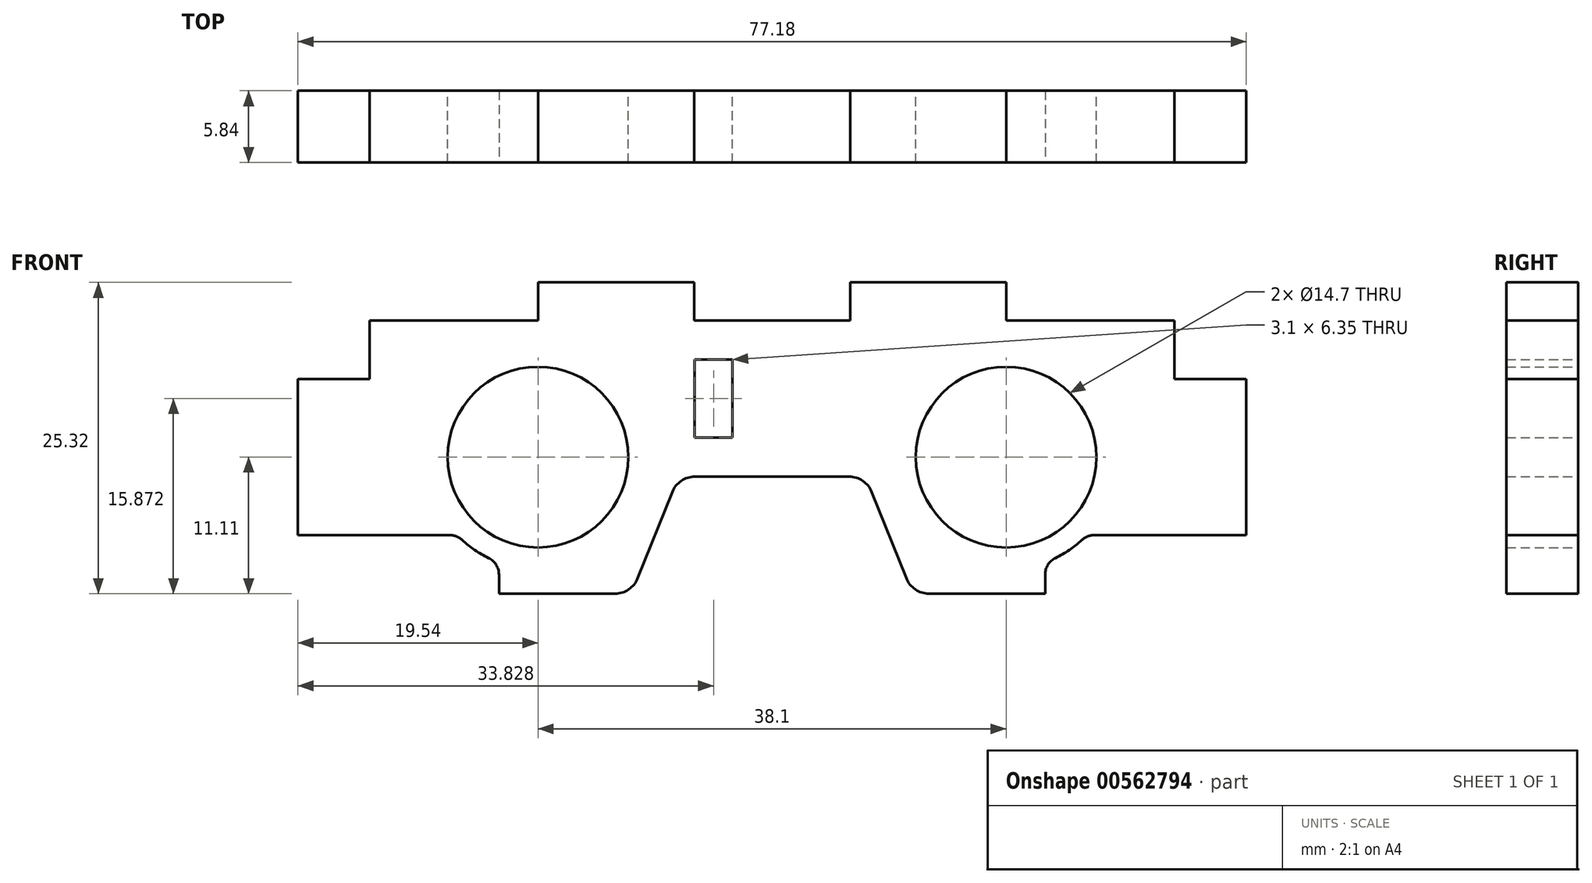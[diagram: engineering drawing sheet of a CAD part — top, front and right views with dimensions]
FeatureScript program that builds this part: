
annotation { "Feature Type Name" : "Feature", "Feature Type Description" : "" }
export const myFeature = defineFeature(function(context is Context, id is Id, definition is map)
    precondition{}
    {
        {
            var Q0;
            Q0=qCreatedBy(makeId("Front.planeOp"),FACE);
            var sketch = newSketch(context, id + "F0", { "sketchPlane" : qUnion([Q0])});
            skCircle(sketch, "E0", {"center": v(-19.05, 0) * mm, "radius": 7.35 * mm});
            skCircle(sketch, "E1.MirrorC", {"center": v(19.05, 0) * mm, "radius": 7.35 * mm});
            skLineSegment(sketch, "E2.bottom", {"start": v(-31.75, 11.11) * mm, "end": v(31.75, 11.11) * mm});
            skLineSegment(sketch, "E2.top", {"start": v(-31.75, -11.11) * mm, "end": v(-11.43, -11.11) * mm});
            skLineSegment(sketch, "E2.left", {"start": v(-31.75, 11.11) * mm, "end": v(-31.75, -11.11) * mm});
            skLineSegment(sketch, "E2.right", {"start": v(31.75, 11.11) * mm, "end": v(31.75, -11.11) * mm});
            skPoint(sketch, "E2.middle", {"position": v(0, 0) * mm});
            skLineSegment(sketch, "E3", {"start": v(-11.43, -11.11) * mm, "end": v(-7.62, -1.59) * mm});
            skLineSegment(sketch, "E4", {"start": v(-7.62, -1.59) * mm, "end": v(0, -1.59) * mm});
            skLineSegment(sketch, "E5.MirrorCS", {"start": v(7.62, -1.59) * mm, "end": v(0, -1.59) * mm});
            skLineSegment(sketch, "E6.MirrorCS", {"start": v(11.43, -11.11) * mm, "end": v(7.62, -1.59) * mm});
            skLineSegment(sketch, "E7.trimOffspring", {"start": v(11.43, -11.11) * mm, "end": v(31.75, -11.11) * mm});
            skSolve(sketch);
        }
        {
            var Q0;
            Q0=makeQuery(id+"F0.imprint","IMPRINT",FACE,{"disambiguationData":[TD([[makeQuery(id+"F0.imprint","IMPRINT",EDGE,{"derivedFrom":sQuery(id+"F0.wireOp",EDGE,"E0")}),-1.0]])]});
            extrude(context, id + "F1", {"entities" : qUnion([Q0]), "depth" : 5.84 * mm, "offsetDistance" : 25.4 * mm});
        }
        {
            var Q0;
            Q0=makeQuery(id+"F1.opExtrude","SWEPT_EDGE",EDGE,{"disambiguationData":[OSD([sQuery(id+"F0.wireOp",EDGE,"E2.top"),sQuery(id+"F0.wireOp",EDGE,"E3")])]});
            var Q1;
            Q1=makeQuery(id+"F1.opExtrude","SWEPT_EDGE",EDGE,{"disambiguationData":[OSD([sQuery(id+"F0.wireOp",EDGE,"E3"),sQuery(id+"F0.wireOp",EDGE,"E4")])]});
            var Q2;
            Q2=makeQuery(id+"F1.opExtrude","SWEPT_EDGE",EDGE,{"disambiguationData":[OSD([sQuery(id+"F0.wireOp",EDGE,"E5.MirrorCS"),sQuery(id+"F0.wireOp",EDGE,"E6.MirrorCS")])]});
            var Q3;
            Q3=makeQuery(id+"F1.opExtrude","SWEPT_EDGE",EDGE,{"disambiguationData":[OSD([sQuery(id+"F0.wireOp",EDGE,"E6.MirrorCS"),sQuery(id+"F0.wireOp",EDGE,"E7.trimOffspring")])]});
            fillet(context, id + "F2", {"entities" : qUnion([Q0, Q1, Q2, Q3]), "radius" : 2 * mm, "tangentPropagation" : true, "allowEdgeOverflow" : false});
        }
        {
            var Q0;
            Q0=makeQuery(id+"F1.opExtrude","CAP_FACE",FACE,{"disambiguationData":[OSD([sQuery(id+"F0.wireOp",EDGE,"E0"),sQuery(id+"F0.wireOp",EDGE,"E1.MirrorC"),sQuery(id+"F0.wireOp",EDGE,"E2.bottom"),sQuery(id+"F0.wireOp",EDGE,"E2.top"),sQuery(id+"F0.wireOp",EDGE,"E2.left"),sQuery(id+"F0.wireOp",EDGE,"E2.right"),sQuery(id+"F0.wireOp",EDGE,"E3"),sQuery(id+"F0.wireOp",EDGE,"E4"),sQuery(id+"F0.wireOp",EDGE,"E5.MirrorCS"),sQuery(id+"F0.wireOp",EDGE,"E6.MirrorCS"),sQuery(id+"F0.wireOp",EDGE,"E7.trimOffspring")])],"isStart":true});
            var sketch = newSketch(context, id + "F3", { "sketchPlane" : qUnion([Q0])});
            skLineSegment(sketch, "E8.bottom", {"start": v(6.31, 1.59) * mm, "end": v(3.21, 1.59) * mm});
            skLineSegment(sketch, "E8.top", {"start": v(6.31, 7.94) * mm, "end": v(3.21, 7.94) * mm});
            skLineSegment(sketch, "E8.left", {"start": v(6.31, 1.59) * mm, "end": v(6.31, 7.94) * mm});
            skLineSegment(sketch, "E8.right", {"start": v(3.21, 1.59) * mm, "end": v(3.21, 7.94) * mm});
            skPoint(sketch, "E8.middle", {"position": v(4.76, 4.76) * mm});
            skSolve(sketch);
        }
        {
            var Q0;
            Q0=qSketchRegion(id+"F3",true);
            extrude(context, id + "F4", {"entities" : qUnion([Q0]), "operationType" : NewBodyOperationType.REMOVE, "oppositeDirection" : true, "depth" : 25.4 * mm, "offsetDistance" : 25.4 * mm});
        }
        {
            var Q0;
            Q0=makeQuery(id+"F1.opExtrude","CAP_FACE",FACE,{"disambiguationData":[OSD([sQuery(id+"F0.wireOp",EDGE,"E0"),sQuery(id+"F0.wireOp",EDGE,"E1.MirrorC"),sQuery(id+"F0.wireOp",EDGE,"E2.bottom"),sQuery(id+"F0.wireOp",EDGE,"E2.top"),sQuery(id+"F0.wireOp",EDGE,"E2.left"),sQuery(id+"F0.wireOp",EDGE,"E2.right"),sQuery(id+"F0.wireOp",EDGE,"E3"),sQuery(id+"F0.wireOp",EDGE,"E4"),sQuery(id+"F0.wireOp",EDGE,"E5.MirrorCS"),sQuery(id+"F0.wireOp",EDGE,"E6.MirrorCS"),sQuery(id+"F0.wireOp",EDGE,"E7.trimOffspring")])],"isStart":false});
            var sketch = newSketch(context, id + "F5", { "sketchPlane" : qUnion([Q0])});
            skLineSegment(sketch, "E9.bottom", {"start": v(-19.05, 11.11) * mm, "end": v(-6.35, 11.11) * mm});
            skLineSegment(sketch, "E9.top", {"start": v(-19.05, 14.21) * mm, "end": v(-6.35, 14.21) * mm});
            skLineSegment(sketch, "E9.left", {"start": v(-19.05, 11.11) * mm, "end": v(-19.05, 14.21) * mm});
            skLineSegment(sketch, "E9.right", {"start": v(-6.35, 11.11) * mm, "end": v(-6.35, 14.21) * mm});
            skPoint(sketch, "E9.middle", {"position": v(-12.7, 12.66) * mm});
            skLineSegment(sketch, "E10.MirrorCS", {"start": v(19.05, 11.11) * mm, "end": v(19.05, 14.21) * mm});
            skLineSegment(sketch, "E11.MirrorCS", {"start": v(19.05, 14.21) * mm, "end": v(6.35, 14.21) * mm});
            skLineSegment(sketch, "E12.MirrorCS", {"start": v(19.05, 11.11) * mm, "end": v(6.35, 11.11) * mm});
            skPoint(sketch, "E13.MirrorP", {"position": v(12.7, 12.66) * mm});
            skLineSegment(sketch, "E14.MirrorCS", {"start": v(6.35, 11.11) * mm, "end": v(6.35, 14.21) * mm});
            skSolve(sketch);
        }
        {
            var Q0;
            Q0=qSketchRegion(id+"F5",true);
            var Q1;
            Q1=makeQuery(id+"F1.opExtrude","CAP_FACE",FACE,{"disambiguationData":[OSD([sQuery(id+"F0.wireOp",EDGE,"E0"),sQuery(id+"F0.wireOp",EDGE,"E1.MirrorC"),sQuery(id+"F0.wireOp",EDGE,"E2.bottom"),sQuery(id+"F0.wireOp",EDGE,"E2.top"),sQuery(id+"F0.wireOp",EDGE,"E2.left"),sQuery(id+"F0.wireOp",EDGE,"E2.right"),sQuery(id+"F0.wireOp",EDGE,"E3"),sQuery(id+"F0.wireOp",EDGE,"E4"),sQuery(id+"F0.wireOp",EDGE,"E5.MirrorCS"),sQuery(id+"F0.wireOp",EDGE,"E6.MirrorCS"),sQuery(id+"F0.wireOp",EDGE,"E7.trimOffspring")])],"isStart":true});
            extrude(context, id + "F6", {"entities" : qUnion([Q0]), "operationType" : NewBodyOperationType.ADD, "endBound" : BoundingType.UP_TO_SURFACE, "oppositeDirection" : true, "depth" : 25.4 * mm, "endBoundEntityFace" : qUnion([Q1]), "offsetDistance" : 25.4 * mm});
        }
        {
            var Q0;
            Q0=makeQuery(id+"F6.boolean.opBoolean","MERGE",FACE,{"derivedFrom":[makeQuery(id+"F1.opExtrude","CAP_FACE",FACE,{"disambiguationData":[OSD([sQuery(id+"F0.wireOp",EDGE,"E0"),sQuery(id+"F0.wireOp",EDGE,"E1.MirrorC"),sQuery(id+"F0.wireOp",EDGE,"E2.bottom"),sQuery(id+"F0.wireOp",EDGE,"E2.top"),sQuery(id+"F0.wireOp",EDGE,"E2.left"),sQuery(id+"F0.wireOp",EDGE,"E2.right"),sQuery(id+"F0.wireOp",EDGE,"E3"),sQuery(id+"F0.wireOp",EDGE,"E4"),sQuery(id+"F0.wireOp",EDGE,"E5.MirrorCS"),sQuery(id+"F0.wireOp",EDGE,"E6.MirrorCS"),sQuery(id+"F0.wireOp",EDGE,"E7.trimOffspring")])],"isStart":false}),makeQuery(id+"F6.opExtrude","CAP_FACE",FACE,{"disambiguationData":[OSD([sQuery(id+"F5.wireOp",EDGE,"E9.bottom"),sQuery(id+"F5.wireOp",EDGE,"E9.top"),sQuery(id+"F5.wireOp",EDGE,"E9.left"),sQuery(id+"F5.wireOp",EDGE,"E9.right")])],"isStart":true}),makeQuery(id+"F6.opExtrude","CAP_FACE",FACE,{"disambiguationData":[OSD([sQuery(id+"F5.wireOp",EDGE,"E10.MirrorCS"),sQuery(id+"F5.wireOp",EDGE,"E11.MirrorCS"),sQuery(id+"F5.wireOp",EDGE,"E12.MirrorCS"),sQuery(id+"F5.wireOp",EDGE,"E14.MirrorCS")])],"isStart":true})]});
            var sketch = newSketch(context, id + "F7", { "sketchPlane" : qUnion([Q0])});
            skLineSegment(sketch, "E15.bottom", {"start": v(32.75, 6.35) * mm, "end": v(38.6, 6.35) * mm});
            skLineSegment(sketch, "E15.top", {"start": v(32.75, -6.35) * mm, "end": v(38.6, -6.35) * mm});
            skLineSegment(sketch, "E15.left", {"start": v(31.75, 6.35) * mm, "end": v(31.75, -6.35) * mm});
            skLineSegment(sketch, "E15.right", {"start": v(38.6, 6.35) * mm, "end": v(38.6, -6.35) * mm});
            skPoint(sketch, "E15.middle", {"position": v(35.17, 0) * mm});
            skPoint(sketch, "E16.MirrorP", {"position": v(-35.17, 0) * mm});
            skLineSegment(sketch, "E17.bottom", {"start": v(31.75, 11.11) * mm, "end": v(32.75, 11.11) * mm});
            skLineSegment(sketch, "E17.top", {"start": v(31.75, -11.11) * mm, "end": v(32.75, -11.11) * mm});
            skLineSegment(sketch, "E17.left", {"start": v(31.75, 11.11) * mm, "end": v(31.75, -11.11) * mm});
            skLineSegment(sketch, "E17.right", {"start": v(32.75, 11.11) * mm, "end": v(32.75, 6.35) * mm});
            skLineSegment(sketch, "E18.trimOffspring", {"start": v(32.75, -6.35) * mm, "end": v(32.75, -11.11) * mm});
            skPoint(sketch, "E19.MirrorCS.start.orphan", {"position": v(-38.6, 6.35) * mm});
            skPoint(sketch, "E20.MirrorCS.start.orphan", {"position": v(-31.75, 6.35) * mm});
            skPoint(sketch, "E21.MirrorCS.end.orphan", {"position": v(-38.6, -6.35) * mm});
            skPoint(sketch, "E21.MirrorCS.start.orphan", {"position": v(-31.75, -6.35) * mm});
            skLineSegment(sketch, "E22.MirrorCS", {"start": v(-31.75, 11.11) * mm, "end": v(-32.75, 11.11) * mm});
            skLineSegment(sketch, "E23.MirrorCS", {"start": v(-31.75, -11.11) * mm, "end": v(-32.75, -11.11) * mm});
            skLineSegment(sketch, "E24.MirrorCS", {"start": v(-31.75, 6.35) * mm, "end": v(-31.75, -6.35) * mm});
            skLineSegment(sketch, "E25.MirrorCS", {"start": v(-32.75, -6.35) * mm, "end": v(-32.75, -11.11) * mm});
            skLineSegment(sketch, "E26.MirrorCS", {"start": v(-32.75, 11.11) * mm, "end": v(-32.75, 6.35) * mm});
            skLineSegment(sketch, "E27.MirrorCS", {"start": v(-32.75, -6.35) * mm, "end": v(-38.6, -6.35) * mm});
            skLineSegment(sketch, "E28.MirrorCS", {"start": v(-32.75, 6.35) * mm, "end": v(-38.6, 6.35) * mm});
            skLineSegment(sketch, "E29.MirrorCS", {"start": v(-38.6, 6.35) * mm, "end": v(-38.6, -6.35) * mm});
            skLineSegment(sketch, "E30.MirrorCS", {"start": v(-31.75, 11.11) * mm, "end": v(-31.75, -11.11) * mm});
            skSolve(sketch);
        }
        {
            var Q0;
            Q0=qSketchRegion(id+"F7",true);
            var Q1;
            {var subQ0=sQuery(id+"F0.wireOp",EDGE,"E7.trimOffspring");var subQ1=sQuery(id+"F0.wireOp",EDGE,"E6.MirrorCS");var subQ2=sQuery(id+"F0.wireOp",EDGE,"E5.MirrorCS");var subQ3=sQuery(id+"F0.wireOp",EDGE,"E4");var subQ4=sQuery(id+"F0.wireOp",EDGE,"E3");var subQ5=sQuery(id+"F0.wireOp",EDGE,"E2.right");var subQ6=sQuery(id+"F0.wireOp",EDGE,"E2.left");var subQ7=sQuery(id+"F0.wireOp",EDGE,"E2.top");var subQ8=sQuery(id+"F0.wireOp",EDGE,"E2.bottom");var subQ9=sQuery(id+"F0.wireOp",EDGE,"E1.MirrorC");var subQ10=sQuery(id+"F0.wireOp",EDGE,"E0");Q1=makeQuery(id+"F6.boolean.opBoolean","MERGE",FACE,{"derivedFrom":[makeQuery(id+"F1.opExtrude","CAP_FACE",FACE,{"disambiguationData":[OSD([subQ10,subQ9,subQ8,subQ7,subQ6,subQ5,subQ4,subQ3,subQ2,subQ1,subQ0])],"isStart":true}),makeQuery(id+"F6.opExtrude","CAP_FACE",FACE,{"disambiguationData":[OSD([subQ10,subQ9,subQ8,subQ7,subQ6,subQ5,subQ4,subQ3,subQ2,subQ1,subQ0]),OD(0.0)],"isStart":false}),makeQuery(id+"F6.opExtrude","CAP_FACE",FACE,{"disambiguationData":[OSD([subQ10,subQ9,subQ8,subQ7,subQ6,subQ5,subQ4,subQ3,subQ2,subQ1,subQ0]),OD(1.0)],"isStart":false})]});}
            extrude(context, id + "F8", {"entities" : qUnion([Q0]), "operationType" : NewBodyOperationType.ADD, "endBound" : BoundingType.UP_TO_SURFACE, "oppositeDirection" : true, "depth" : 25.4 * mm, "endBoundEntityFace" : qUnion([Q1]), "offsetDistance" : 25.4 * mm});
        }
        {
            var Q0;
            Q0=makeQuery(id+"F8.boolean.opBoolean","MERGE",FACE,{"derivedFrom":[makeQuery(id+"F6.boolean.opBoolean","MERGE",FACE,{"derivedFrom":[makeQuery(id+"F1.opExtrude","CAP_FACE",FACE,{"disambiguationData":[OSD([sQuery(id+"F0.wireOp",EDGE,"E0"),sQuery(id+"F0.wireOp",EDGE,"E1.MirrorC"),sQuery(id+"F0.wireOp",EDGE,"E2.bottom"),sQuery(id+"F0.wireOp",EDGE,"E2.top"),sQuery(id+"F0.wireOp",EDGE,"E2.left"),sQuery(id+"F0.wireOp",EDGE,"E2.right"),sQuery(id+"F0.wireOp",EDGE,"E3"),sQuery(id+"F0.wireOp",EDGE,"E4"),sQuery(id+"F0.wireOp",EDGE,"E5.MirrorCS"),sQuery(id+"F0.wireOp",EDGE,"E6.MirrorCS"),sQuery(id+"F0.wireOp",EDGE,"E7.trimOffspring")])],"isStart":false}),makeQuery(id+"F6.opExtrude","CAP_FACE",FACE,{"disambiguationData":[OSD([sQuery(id+"F5.wireOp",EDGE,"E9.bottom"),sQuery(id+"F5.wireOp",EDGE,"E9.top"),sQuery(id+"F5.wireOp",EDGE,"E9.left"),sQuery(id+"F5.wireOp",EDGE,"E9.right")])],"isStart":true}),makeQuery(id+"F6.opExtrude","CAP_FACE",FACE,{"disambiguationData":[OSD([sQuery(id+"F5.wireOp",EDGE,"E10.MirrorCS"),sQuery(id+"F5.wireOp",EDGE,"E11.MirrorCS"),sQuery(id+"F5.wireOp",EDGE,"E12.MirrorCS"),sQuery(id+"F5.wireOp",EDGE,"E14.MirrorCS")])],"isStart":true})]}),makeQuery(id+"F8.opExtrude","CAP_FACE",FACE,{"disambiguationData":[OSD([sQuery(id+"F7.wireOp",EDGE,"E15.bottom"),sQuery(id+"F7.wireOp",EDGE,"E15.top"),sQuery(id+"F7.wireOp",EDGE,"E15.right"),sQuery(id+"F7.wireOp",EDGE,"E17.bottom"),sQuery(id+"F7.wireOp",EDGE,"E17.top"),sQuery(id+"F7.wireOp",EDGE,"E17.left"),sQuery(id+"F7.wireOp",EDGE,"E17.right"),sQuery(id+"F7.wireOp",EDGE,"E18.trimOffspring")])],"isStart":true}),makeQuery(id+"F8.opExtrude","CAP_FACE",FACE,{"disambiguationData":[OSD([sQuery(id+"F7.wireOp",EDGE,"E22.MirrorCS"),sQuery(id+"F7.wireOp",EDGE,"E23.MirrorCS"),sQuery(id+"F7.wireOp",EDGE,"E25.MirrorCS"),sQuery(id+"F7.wireOp",EDGE,"E26.MirrorCS"),sQuery(id+"F7.wireOp",EDGE,"E27.MirrorCS"),sQuery(id+"F7.wireOp",EDGE,"E28.MirrorCS"),sQuery(id+"F7.wireOp",EDGE,"E29.MirrorCS"),sQuery(id+"F7.wireOp",EDGE,"E30.MirrorCS")])],"isStart":true})]});
            var sketch = newSketch(context, id + "F9", { "sketchPlane" : qUnion([Q0])});
            skLineSegment(sketch, "E31", {"start": v(-22.22, -8.57) * mm, "end": v(-22.22, -11.11) * mm});
            skLineSegment(sketch, "E32", {"start": v(-32.75, -8.57) * mm, "end": v(-32.75, -11.11) * mm});
            skLineSegment(sketch, "E33", {"start": v(-32.75, -11.11) * mm, "end": v(-22.22, -11.11) * mm});
            skArc(sketch, "E34", {"start": v(-25.63, -6.35) * mm, "mid": v(-24.05, -7.65) * mm, "end": v(-22.22, -8.57) * mm});
            skLineSegment(sketch, "E35", {"start": v(-32.75, -6.35) * mm, "end": v(-25.63, -6.35) * mm});
            skPoint(sketch, "E36.MirrorCS.start.orphan", {"position": v(22.22, -8.57) * mm});
            skPoint(sketch, "E37.MirrorCS.start.orphan", {"position": v(32.75, -8.57) * mm});
            skPoint(sketch, "E38.MirrorCS.end.orphan", {"position": v(22.22, -11.11) * mm});
            skPoint(sketch, "E38.MirrorCS.start.orphan", {"position": v(32.75, -11.11) * mm});
            skLineSegment(sketch, "E39.MirrorCS", {"start": v(32.75, -6.35) * mm, "end": v(25.63, -6.35) * mm});
            skArc(sketch, "E40.MirrorCS", {"start": v(25.63, -6.35) * mm, "mid": v(24.05, -7.65) * mm, "end": v(22.22, -8.57) * mm});
            skLineSegment(sketch, "E41.MirrorCS", {"start": v(22.22, -8.57) * mm, "end": v(22.22, -11.11) * mm});
            skLineSegment(sketch, "E42.MirrorCS", {"start": v(32.75, -8.57) * mm, "end": v(32.75, -11.11) * mm});
            skLineSegment(sketch, "E43.MirrorCS", {"start": v(32.75, -11.11) * mm, "end": v(22.22, -11.11) * mm});
            skLineSegment(sketch, "E44", {"start": v(-32.75, -8.57) * mm, "end": v(-32.75, -6.35) * mm});
            skLineSegment(sketch, "E45", {"start": v(32.75, -8.57) * mm, "end": v(32.75, -6.35) * mm});
            skSolve(sketch);
        }
        {
            var Q0;
            Q0 = qSketchRegion(id + "F9", true);
            extrude(context, id + "F10", {"entities" : qUnion([Q0]), "operationType" : NewBodyOperationType.REMOVE, "oppositeDirection" : true, "depth" : 25.4 * mm, "offsetDistance" : 25.4 * mm});
        }
        {
            var Q0;
            Q0=makeQuery(id+"F10.boolean.opBoolean","COPY",EDGE,{"derivedFrom":makeQuery(id+"F10.opExtrude","SWEPT_EDGE",EDGE,{"disambiguationData":[OSD([sQuery(id+"F9.wireOp",EDGE,"E39.MirrorCS"),sQuery(id+"F9.wireOp",EDGE,"E40.MirrorCS")])]})});
            var Q1;
            Q1=makeQuery(id+"F10.boolean.opBoolean","COPY",EDGE,{"derivedFrom":makeQuery(id+"F10.opExtrude","SWEPT_EDGE",EDGE,{"disambiguationData":[OSD([sQuery(id+"F0.wireOp",EDGE,"E7.trimOffspring"),sQuery(id+"F7.wireOp",EDGE,"E17.top"),sQuery(id+"F9.wireOp",EDGE,"E41.MirrorCS"),sQuery(id+"F9.wireOp",EDGE,"E43.MirrorCS")])]})});
            var Q2;
            Q2=makeQuery(id+"F10.boolean.opBoolean","COPY",EDGE,{"derivedFrom":makeQuery(id+"F10.opExtrude","SWEPT_EDGE",EDGE,{"disambiguationData":[OSD([sQuery(id+"F9.wireOp",EDGE,"E40.MirrorCS"),sQuery(id+"F9.wireOp",EDGE,"E41.MirrorCS")])]})});
            var Q3;
            Q3=makeQuery(id+"F10.boolean.opBoolean","COPY",EDGE,{"derivedFrom":makeQuery(id+"F10.opExtrude","SWEPT_EDGE",EDGE,{"disambiguationData":[OSD([sQuery(id+"F9.wireOp",EDGE,"E34"),sQuery(id+"F9.wireOp",EDGE,"E35")])]})});
            var Q4;
            Q4=makeQuery(id+"F10.boolean.opBoolean","COPY",EDGE,{"derivedFrom":makeQuery(id+"F10.opExtrude","SWEPT_EDGE",EDGE,{"disambiguationData":[OSD([sQuery(id+"F9.wireOp",EDGE,"E31"),sQuery(id+"F9.wireOp",EDGE,"E34")])]})});
            var Q5;
            Q5=makeQuery(id+"F10.boolean.opBoolean","COPY",EDGE,{"derivedFrom":makeQuery(id+"F10.opExtrude","SWEPT_EDGE",EDGE,{"disambiguationData":[OSD([sQuery(id+"F0.wireOp",EDGE,"E2.top"),sQuery(id+"F7.wireOp",EDGE,"E23.MirrorCS"),sQuery(id+"F9.wireOp",EDGE,"E31"),sQuery(id+"F9.wireOp",EDGE,"E33")])]})});
            fillet(context, id + "F11", {"entities" : qUnion([Q0, Q1, Q2, Q3, Q4, Q5]), "radius" : 1.5 * mm, "tangentPropagation" : true, "allowEdgeOverflow" : false});
        }
    });
